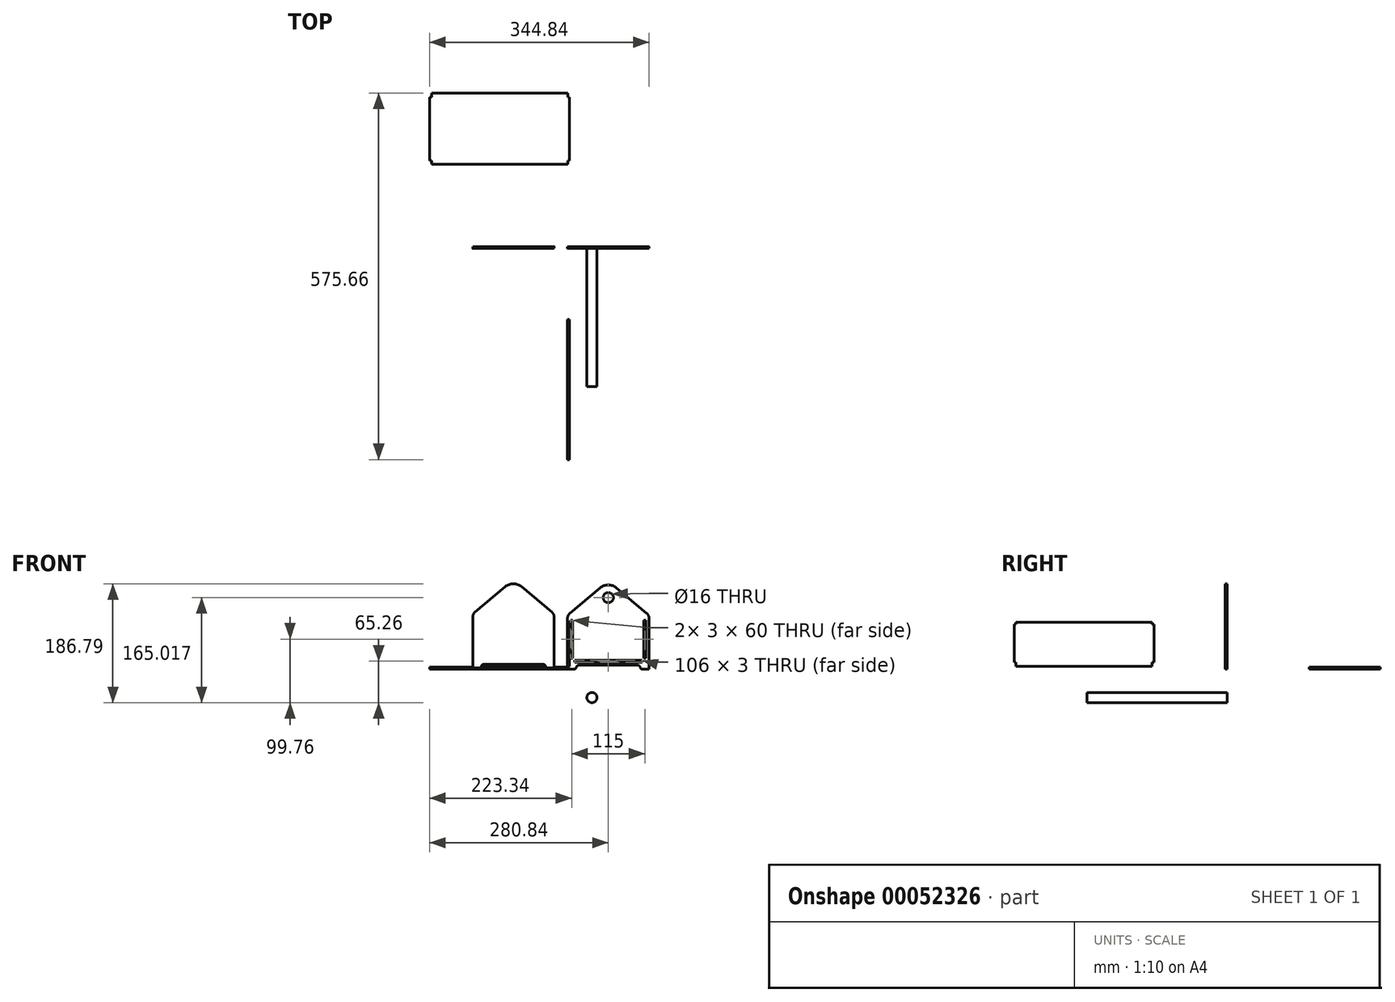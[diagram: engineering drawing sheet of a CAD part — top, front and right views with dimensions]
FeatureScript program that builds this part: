
annotation { "Feature Type Name" : "Feature", "Feature Type Description" : "" }
export const myFeature = defineFeature(function(context is Context, id is Id, definition is map)
    precondition{}
    {
        {
            var Q0;
            Q0=qCreatedBy(makeId("Front.planeOp"),FACE);
            var sketch = newSketch(context, id + "F0", { "sketchPlane" : qUnion([Q0])});
            skLineSegment(sketch, "E0", {"start": v(0, 0) * mm, "end": v(0, 80) * mm});
            skLineSegment(sketch, "E1", {"start": v(3.57, 87.66) * mm, "end": v(51.14, 127.58) * mm});
            skLineSegment(sketch, "E2", {"start": v(76.86, 127.58) * mm, "end": v(124.43, 87.66) * mm});
            skLineSegment(sketch, "E3", {"start": v(128, 80) * mm, "end": v(128, 0) * mm});
            skLineSegment(sketch, "E4", {"start": v(128, 0) * mm, "end": v(116, 0) * mm});
            skLineSegment(sketch, "E5", {"start": v(116, 0) * mm, "end": v(113.7, 4) * mm});
            skLineSegment(sketch, "E6", {"start": v(110.23, 6) * mm, "end": v(17.77, 6) * mm});
            skLineSegment(sketch, "E7", {"start": v(14.3, 4) * mm, "end": v(12, 0) * mm});
            skLineSegment(sketch, "E8", {"start": v(12, 0) * mm, "end": v(0, 0) * mm});
            skPoint(sketch, "E9.visualSharp", {"position": v(64, 138.37) * mm});
            skArc(sketch, "E9.filletArc", {"start": v(76.86, 127.58) * mm, "mid": v(64, 132.26) * mm, "end": v(51.14, 127.58) * mm});
            skCircle(sketch, "E10", {"center": v(64, 112.26) * mm, "radius": 8 * mm});
            skPoint(sketch, "E11.visualSharp", {"position": v(0, 84.66) * mm});
            skArc(sketch, "E11.filletArc", {"start": v(3.57, 87.66) * mm, "mid": v(0.94, 84.23) * mm, "end": v(0, 80) * mm});
            skPoint(sketch, "E12.visualSharp", {"position": v(128, 84.66) * mm});
            skArc(sketch, "E12.filletArc", {"start": v(128, 80) * mm, "mid": v(127.06, 84.23) * mm, "end": v(124.43, 87.66) * mm});
            skPoint(sketch, "E13.visualSharp", {"position": v(15.46, 6) * mm});
            skArc(sketch, "E13.filletArc", {"start": v(17.77, 6) * mm, "mid": v(15.77, 5.46) * mm, "end": v(14.3, 4) * mm});
            skPoint(sketch, "E14.visualSharp", {"position": v(112.54, 6) * mm});
            skArc(sketch, "E14.filletArc", {"start": v(113.7, 4) * mm, "mid": v(112.23, 5.46) * mm, "end": v(110.23, 6) * mm});
            skLineSegment(sketch, "E15.bottom", {"start": v(5, 77) * mm, "end": v(8, 77) * mm});
            skLineSegment(sketch, "E15.top", {"start": v(5, 17) * mm, "end": v(8, 17) * mm});
            skLineSegment(sketch, "E15.left", {"start": v(5, 77) * mm, "end": v(5, 17) * mm});
            skLineSegment(sketch, "E15.right", {"start": v(8, 77) * mm, "end": v(8, 17) * mm});
            skLineSegment(sketch, "E16.bottom", {"start": v(120, 77) * mm, "end": v(123, 77) * mm});
            skLineSegment(sketch, "E16.top", {"start": v(120, 17) * mm, "end": v(123, 17) * mm});
            skLineSegment(sketch, "E16.left", {"start": v(120, 77) * mm, "end": v(120, 17) * mm});
            skLineSegment(sketch, "E16.right", {"start": v(123, 77) * mm, "end": v(123, 17) * mm});
            skLineSegment(sketch, "E17.bottom", {"start": v(11, 14) * mm, "end": v(117, 14) * mm});
            skLineSegment(sketch, "E17.top", {"start": v(11, 11) * mm, "end": v(117, 11) * mm});
            skLineSegment(sketch, "E17.left", {"start": v(11, 14) * mm, "end": v(11, 11) * mm});
            skLineSegment(sketch, "E17.right", {"start": v(117, 14) * mm, "end": v(117, 11) * mm});
            skSolve(sketch);
        }
        {
            var Q0;
            Q0 = qSketchRegion(id + "F0", true);
            extrude(context, id + "F1", {"entities" : qUnion([Q0]), "depth" : 3 * mm});
        }
        {
            var Q0;
            Q0=qCreatedBy(makeId("Top.planeOp"),FACE);
            var sketch = newSketch(context, id + "F2", { "sketchPlane" : qUnion([Q0])});
            skLineSegment(sketch, "E18.bottom", {"start": v(-213.84, 241.01) * mm, "end": v(0.16, 241.01) * mm});
            skLineSegment(sketch, "E18.top", {"start": v(-213.6, 129.01) * mm, "end": v(0.16, 129.01) * mm});
            skLineSegment(sketch, "E18.left", {"start": v(-216.84, 235.01) * mm, "end": v(-216.84, 135) * mm});
            skLineSegment(sketch, "E18.right", {"start": v(3.16, 235.01) * mm, "end": v(3.16, 135) * mm});
            skLineSegment(sketch, "E19.top", {"start": v(-216.84, 235.01) * mm, "end": v(-213.84, 235.01) * mm});
            skLineSegment(sketch, "E19.right", {"start": v(-213.84, 241.01) * mm, "end": v(-213.84, 235.01) * mm});
            skLineSegment(sketch, "E20.bottom", {"start": v(-216.84, 135) * mm, "end": v(-213.84, 135) * mm});
            skLineSegment(sketch, "E20.right", {"start": v(-213.84, 135) * mm, "end": v(-213.6, 129.01) * mm});
            skLineSegment(sketch, "E21.top", {"start": v(0.16, 235.01) * mm, "end": v(3.16, 235.01) * mm});
            skLineSegment(sketch, "E21.left", {"start": v(0.16, 241.01) * mm, "end": v(0.16, 235.01) * mm});
            skLineSegment(sketch, "E22", {"start": v(0.16, 129.01) * mm, "end": v(0.16, 135) * mm});
            skLineSegment(sketch, "E23", {"start": v(0.16, 135) * mm, "end": v(3.16, 135) * mm});
            skSolve(sketch);
        }
        {
            var Q0;
            Q0=makeQuery(id+"F2.imprint","IMPRINT",FACE,{"disambiguationData":[TD([[makeQuery(id+"F2.imprint","IMPRINT",EDGE,{"derivedFrom":sQuery(id+"F2.wireOp",EDGE,"E18.bottom")}),-1.0]])]});
            extrude(context, id + "F3", {"entities" : qUnion([Q0]), "depth" : 3 * mm});
        }
        {
            var Q0;
            Q0=qCreatedBy(makeId("Front.planeOp"),FACE);
            var sketch = newSketch(context, id + "F4", { "sketchPlane" : qUnion([Q0])});
            skLineSegment(sketch, "E24", {"start": v(-875.51, 246.44) * mm, "end": v(-875.51, 326.44) * mm});
            skLineSegment(sketch, "E25", {"start": v(-871.94, 334.1) * mm, "end": v(-824.37, 374.02) * mm});
            skLineSegment(sketch, "E26", {"start": v(-798.66, 374.02) * mm, "end": v(-751.08, 334.1) * mm});
            skLineSegment(sketch, "E27", {"start": v(-747.51, 326.44) * mm, "end": v(-747.51, 246.44) * mm});
            skLineSegment(sketch, "E28", {"start": v(-747.51, 246.44) * mm, "end": v(-759.51, 246.44) * mm});
            skLineSegment(sketch, "E29", {"start": v(-759.51, 246.44) * mm, "end": v(-761.82, 250.44) * mm});
            skLineSegment(sketch, "E30", {"start": v(-765.28, 252.44) * mm, "end": v(-857.74, 252.44) * mm});
            skLineSegment(sketch, "E31", {"start": v(-861.2, 250.44) * mm, "end": v(-863.51, 246.44) * mm});
            skLineSegment(sketch, "E32", {"start": v(-863.51, 246.44) * mm, "end": v(-875.51, 246.44) * mm});
            skPoint(sketch, "E33.visualSharp", {"position": v(-811.51, 384.8) * mm});
            skArc(sketch, "E33.filletArc", {"start": v(-798.66, 374.02) * mm, "mid": v(-811.51, 378.7) * mm, "end": v(-824.37, 374.02) * mm});
            skCircle(sketch, "E34", {"center": v(-811.51, 358.7) * mm, "radius": 8 * mm});
            skPoint(sketch, "E35.visualSharp", {"position": v(-875.51, 331.1) * mm});
            skArc(sketch, "E35.filletArc", {"start": v(-871.94, 334.1) * mm, "mid": v(-874.57, 330.66) * mm, "end": v(-875.51, 326.44) * mm});
            skPoint(sketch, "E36.visualSharp", {"position": v(-747.51, 331.1) * mm});
            skArc(sketch, "E36.filletArc", {"start": v(-747.51, 326.44) * mm, "mid": v(-748.45, 330.66) * mm, "end": v(-751.08, 334.1) * mm});
            skPoint(sketch, "E37.visualSharp", {"position": v(-860.05, 252.44) * mm});
            skArc(sketch, "E37.filletArc", {"start": v(-857.74, 252.44) * mm, "mid": v(-859.74, 251.9) * mm, "end": v(-861.2, 250.44) * mm});
            skPoint(sketch, "E38.visualSharp", {"position": v(-762.98, 252.44) * mm});
            skArc(sketch, "E38.filletArc", {"start": v(-761.82, 250.44) * mm, "mid": v(-763.28, 251.9) * mm, "end": v(-765.28, 252.44) * mm});
            skLineSegment(sketch, "E39.bottom", {"start": v(-870.51, 323.44) * mm, "end": v(-867.51, 323.44) * mm});
            skLineSegment(sketch, "E39.top", {"start": v(-870.51, 263.44) * mm, "end": v(-867.51, 263.44) * mm});
            skLineSegment(sketch, "E39.left", {"start": v(-870.51, 323.44) * mm, "end": v(-870.51, 263.44) * mm});
            skLineSegment(sketch, "E39.right", {"start": v(-867.51, 323.44) * mm, "end": v(-867.51, 263.44) * mm});
            skLineSegment(sketch, "E40.bottom", {"start": v(-755.51, 323.44) * mm, "end": v(-752.51, 323.44) * mm});
            skLineSegment(sketch, "E40.top", {"start": v(-755.51, 263.44) * mm, "end": v(-752.51, 263.44) * mm});
            skLineSegment(sketch, "E40.left", {"start": v(-755.51, 323.44) * mm, "end": v(-755.51, 263.44) * mm});
            skLineSegment(sketch, "E40.right", {"start": v(-752.51, 323.44) * mm, "end": v(-752.51, 263.44) * mm});
            skLineSegment(sketch, "E41.bottom", {"start": v(-864.51, 260.44) * mm, "end": v(-758.51, 260.44) * mm});
            skLineSegment(sketch, "E41.top", {"start": v(-864.51, 257.44) * mm, "end": v(-758.51, 257.44) * mm});
            skLineSegment(sketch, "E41.left", {"start": v(-864.51, 260.44) * mm, "end": v(-864.51, 257.44) * mm});
            skLineSegment(sketch, "E41.right", {"start": v(-758.51, 260.44) * mm, "end": v(-758.51, 257.44) * mm});
            skLineSegment(sketch, "E42", {"start": v(-149.04, 1.78) * mm, "end": v(-149.04, 81.78) * mm});
            skLineSegment(sketch, "E43", {"start": v(-145.47, 89.44) * mm, "end": v(-97.9, 129.35) * mm});
            skLineSegment(sketch, "E44", {"start": v(-72.18, 129.35) * mm, "end": v(-24.61, 89.44) * mm});
            skLineSegment(sketch, "E45", {"start": v(-21.04, 81.78) * mm, "end": v(-21.04, 1.78) * mm});
            skLineSegment(sketch, "E46", {"start": v(-21.04, 1.78) * mm, "end": v(-33.04, 1.78) * mm});
            skLineSegment(sketch, "E47", {"start": v(-33.04, 1.78) * mm, "end": v(-35.35, 5.78) * mm});
            skLineSegment(sketch, "E48", {"start": v(-38.81, 7.78) * mm, "end": v(-131.26, 7.78) * mm});
            skLineSegment(sketch, "E49", {"start": v(-134.73, 5.78) * mm, "end": v(-137.04, 1.78) * mm});
            skLineSegment(sketch, "E50", {"start": v(-137.04, 1.78) * mm, "end": v(-149.04, 1.78) * mm});
            skPoint(sketch, "E51.visualSharp", {"position": v(-85.04, 140.14) * mm});
            skArc(sketch, "E51.filletArc", {"start": v(-72.18, 129.35) * mm, "mid": v(-85.04, 134.03) * mm, "end": v(-97.9, 129.35) * mm});
            skPoint(sketch, "E52.visualSharp", {"position": v(-149.04, 86.44) * mm});
            skArc(sketch, "E52.filletArc", {"start": v(-145.47, 89.44) * mm, "mid": v(-148.1, 86) * mm, "end": v(-149.04, 81.78) * mm});
            skPoint(sketch, "E53.visualSharp", {"position": v(-21.04, 86.44) * mm});
            skArc(sketch, "E53.filletArc", {"start": v(-21.04, 81.78) * mm, "mid": v(-21.98, 86) * mm, "end": v(-24.61, 89.44) * mm});
            skPoint(sketch, "E54.visualSharp", {"position": v(-133.57, 7.78) * mm});
            skArc(sketch, "E54.filletArc", {"start": v(-131.26, 7.78) * mm, "mid": v(-133.26, 7.24) * mm, "end": v(-134.73, 5.78) * mm});
            skPoint(sketch, "E55.visualSharp", {"position": v(-36.5, 7.78) * mm});
            skArc(sketch, "E55.filletArc", {"start": v(-35.35, 5.78) * mm, "mid": v(-36.81, 7.24) * mm, "end": v(-38.81, 7.78) * mm});
            skSolve(sketch);
        }
        {
            var Q0;
            Q0=makeQuery(id+"F4.imprint","IMPRINT",FACE,{"disambiguationData":[TD([[makeQuery(id+"F4.imprint","IMPRINT",EDGE,{"derivedFrom":sQuery(id+"F4.wireOp",EDGE,"E42")}),-1.0]])]});
            extrude(context, id + "F5", {"entities" : qUnion([Q0]), "depth" : 3 * mm});
        }
        {
            var Q0;
            Q0=qCreatedBy(makeId("Front.planeOp"),FACE);
            var sketch = newSketch(context, id + "F6", { "sketchPlane" : qUnion([Q0])});
            skCircle(sketch, "E56", {"center": v(38.25, -44.76) * mm, "radius": 8 * mm});
            skSolve(sketch);
        }
        {
            var Q0;
            Q0 = qSketchRegion(id + "F6", true);
            extrude(context, id + "F7", {"entities" : qUnion([Q0]), "depth" : 220 * mm});
        }
        {
            var Q0;
            Q0=qCreatedBy(makeId("Right.planeOp"),FACE);
            var sketch = newSketch(context, id + "F8", { "sketchPlane" : qUnion([Q0])});
            skLineSegment(sketch, "E57.bottom", {"start": v(-117.65, 73.56) * mm, "end": v(-331.65, 73.56) * mm});
            skLineSegment(sketch, "E57.top", {"start": v(-117.58, 4.56) * mm, "end": v(-331.6, 4.56) * mm});
            skLineSegment(sketch, "E57.left", {"start": v(-114.65, 70.56) * mm, "end": v(-114.65, 10.56) * mm});
            skLineSegment(sketch, "E57.right", {"start": v(-334.65, 70.56) * mm, "end": v(-334.65, 10.56) * mm});
            skLineSegment(sketch, "E58.top", {"start": v(-334.65, 10.56) * mm, "end": v(-331.65, 10.56) * mm});
            skLineSegment(sketch, "E58.right", {"start": v(-331.6, 4.56) * mm, "end": v(-331.65, 10.56) * mm});
            skLineSegment(sketch, "E59.top", {"start": v(-114.65, 10.56) * mm, "end": v(-117.65, 10.56) * mm});
            skLineSegment(sketch, "E59.right", {"start": v(-117.58, 4.56) * mm, "end": v(-117.65, 10.56) * mm});
            skLineSegment(sketch, "E60.top", {"start": v(-114.65, 70.56) * mm, "end": v(-117.65, 70.56) * mm});
            skLineSegment(sketch, "E60.right", {"start": v(-117.65, 73.56) * mm, "end": v(-117.65, 70.56) * mm});
            skLineSegment(sketch, "E61.top", {"start": v(-334.65, 70.56) * mm, "end": v(-331.65, 70.56) * mm});
            skLineSegment(sketch, "E61.right", {"start": v(-331.65, 73.56) * mm, "end": v(-331.65, 70.56) * mm});
            skSolve(sketch);
        }
        {
            var Q0;
            Q0=makeQuery(id+"F8.imprint","IMPRINT",FACE,{"disambiguationData":[TD([[makeQuery(id+"F8.imprint","IMPRINT",EDGE,{"derivedFrom":sQuery(id+"F8.wireOp",EDGE,"E57.bottom")}),1.0]])]});
            extrude(context, id + "F9", {"entities" : qUnion([Q0]), "depth" : 3 * mm});
        }
    });
